# Revit family: Hydrablock 5-7-9 M
name_source: partatom
category: Attrezzatura meccanica
units: mm (PartAtom-declared; Revit-internal decimal feet)

## family parameters
Basato su piano di lavoro = No
Condiviso = No
Mantieni orientamento annotazione = No
Numero OmniClass = 23.75.00.00
Punto di calcolo locali = No
Quota connettore circolare = Usa diametro
Sempre verticale = Sì
Taglio con vuoti quando caricato = No
Tipo di parte = Normale
Titolo OmniClass = Climate Control (HVAC)

## types (3) — shared parameters
Air Flow = 3050 m³/h
Casing color = SB2014
Compressor = 1
Condensation = air
Depth = 402 mm
Descrizione = High efficiency air cooled
Drain piping = 16 mm
Gas = R32
Height = 945 mm  [stored 3.10039 ft]
Installation = Outdoor installation
MOP (Maximum overcurrent protection) = 20 A
Machine material = Galvanized Steel
Min cable selection (power wiring) = 3×4 mm2
Minimum Circuit Amps = 14 A
Net Weight = 92.00 kg
Power supply = 220-240V 1N~50Hz
Produttore = Midea
Series = M-Thermal
URL = https://cac.midea.com
Water piping connections = 25 mm  [stored 0.082021 ft]
Width = 1210 mm  [stored 3.96982 ft]
clearance access behind = 300 mm
clearance access front = 1000 mm  [stored 3.28084 ft]
clearance access left = 600 mm
clearance access right = 600 mm
zero-valued in all types: Prospetto di default

## per-type parameters (varying)
| type | Cooling Power Input (EWT 23⁰C, LWT 18⁰C) | Cooling Power Input(EWT 12⁰C, LWT 7⁰C) | Cooling capacity (EWT 12⁰C, LWT 7⁰C) | Cooling capacity (EWT 23⁰C, LWT 18⁰C) | Heating Power Input (EWT 30⁰C, LWT 35⁰C) | Heating Power Input (EWT 40⁰C, LWT 45⁰C) | Heating capacity (EWT 30⁰C, LWT 35⁰C) | Heating capacity (EWT 40⁰C, LWT 45⁰C) | Modello |
| Hydrablock 5 M | 1 kW | 2 kW | 5 kW | 5 kW | 1 kW | 1 kW | 5 kW | 5 kW | MHC-V5W/D2N8 |
| Hydrablock 7 M | 1 kW | 2 kW | 6 kW | 6 kW | 1 kW | 2 kW | 7 kW | 7 kW | MHC-V7W/D2N8 |
| Hydrablock 9 M | 2 kW | 3 kW | 8 kW | 8 kW | 2 kW | 3 kW | 9 kW | 9 kW | MHC-V9W/D2N8 |

note: [stored X ft] marks values corroborated as IEEE doubles in the binary element streams (Revit-internal decimal feet)

## geometry (parser evidence)
native form markers: Sweep x8
no freeform markers — native parametric forms only
